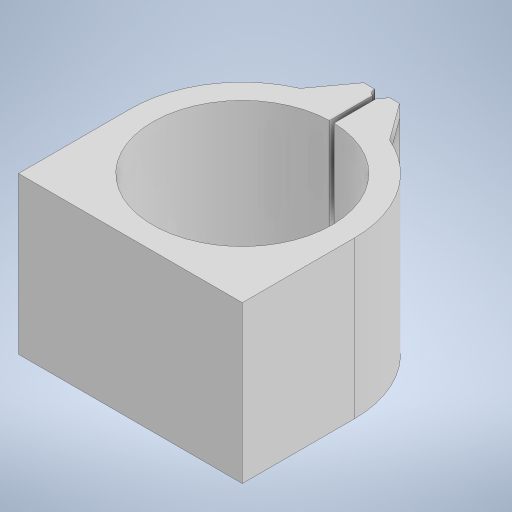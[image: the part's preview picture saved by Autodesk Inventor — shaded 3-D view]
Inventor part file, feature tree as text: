
AUTODESK INVENTOR PART (.ipt)
format: ipt  version: 2024 (Build 280153000, 153)  size: 241,664 bytes
history: native  units: mm
features: extrude x4, sketch x4
ambient origin geometry x8: Origin, YZ Plane, XZ Plane, XY Plane, X Axis, Y Axis, Z Axis, Center Point
bodies: Solid1 (feature_tree)
feature tree (8):
  extrude  "Extrusion1"  Depth=70.0mm TaperAngle=0.0deg
  extrude  "Extrusion2"  TaperAngle=0.0deg  [1 undecoded]
  extrude  "Extrusion3"  Depth=6.1mm
  extrude  "Extrusion4"  [1 undecoded]
  sketch  "Sketch1"  dims[d0=100.0mm d1=70.0mm d2=0.0mm]
  sketch  "Sketch2"  dims[d3=100.0mm d4=0.0mm d5=0.0mm d6=0.0mm]
  sketch  "Sketch3"  dims[d7=6.0mm d8=0.0mm d9=6.1mm]
  sketch  "Sketch4"
note: 2 required parameter values undecoded (feature->parameter linkage not recoverable at this tier; creation-order binding heuristic only, values carry confidence <= 0.55)
